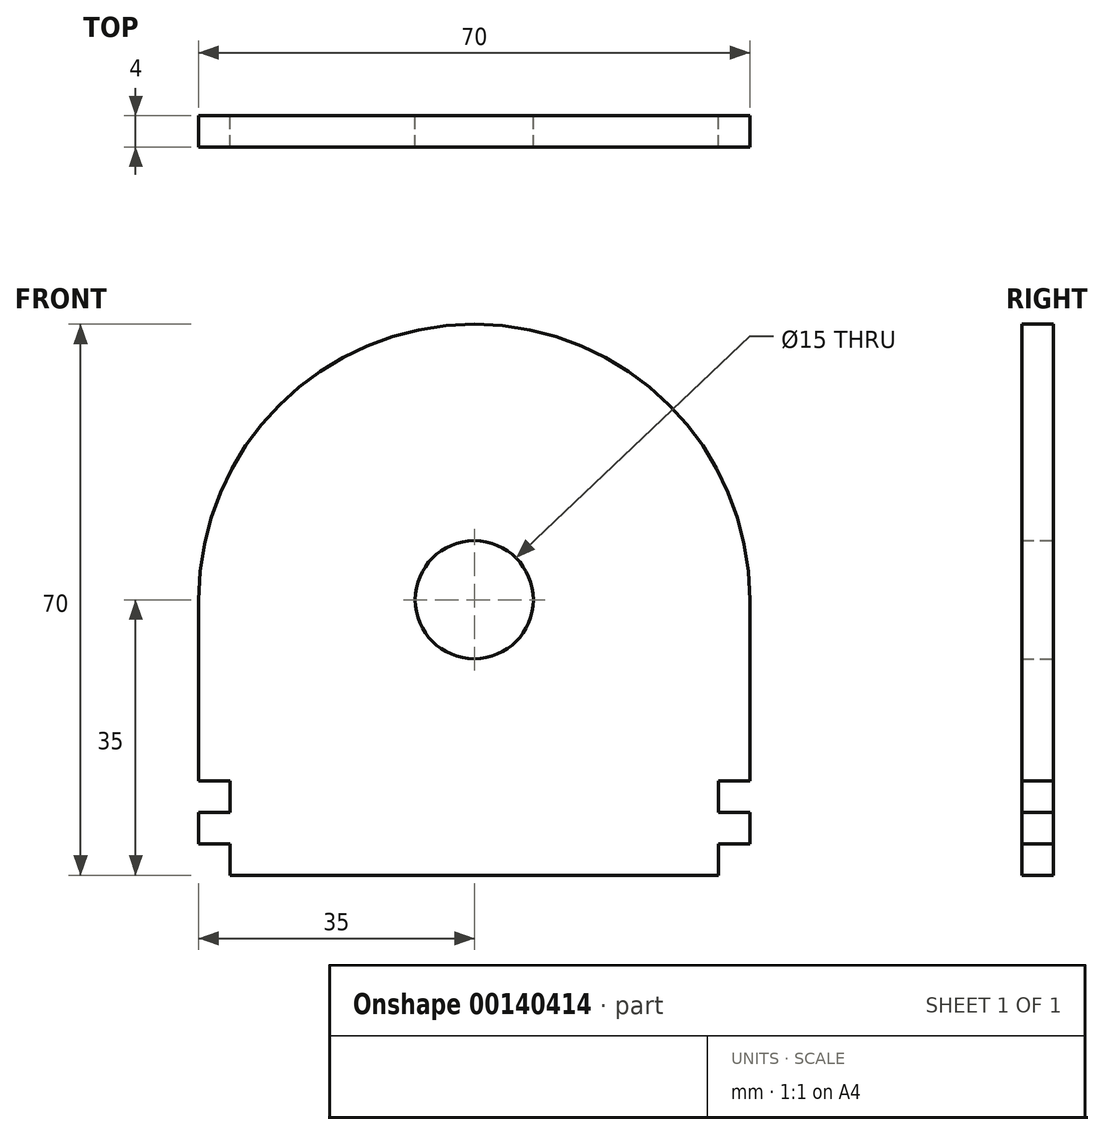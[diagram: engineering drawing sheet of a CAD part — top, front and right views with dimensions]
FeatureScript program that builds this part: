
annotation { "Feature Type Name" : "Feature", "Feature Type Description" : "" }
export const myFeature = defineFeature(function(context is Context, id is Id, definition is map)
    precondition{}
    {
        {
            var Q0;
            Q0=qCreatedBy(makeId("Front.planeOp"),FACE);
            var sketch = newSketch(context, id + "F0", { "sketchPlane" : qUnion([Q0])});
            skCircle(sketch, "E0", {"center": v(0, 0) * mm, "radius": 35 * mm});
            skLineSegment(sketch, "E1", {"start": v(0, -35) * mm, "end": v(35, -35) * mm});
            skLineSegment(sketch, "E2", {"start": v(35, -35) * mm, "end": v(35, 0) * mm});
            skLineSegment(sketch, "E3.MirrorCS", {"start": v(-35, -35) * mm, "end": v(-35, 0) * mm});
            skLineSegment(sketch, "E4.MirrorCS", {"start": v(0, -35) * mm, "end": v(-35, -35) * mm});
            skCircle(sketch, "E5", {"center": v(0, 0) * mm, "radius": 7.5 * mm});
            skLineSegment(sketch, "E6.bottom", {"start": v(-35, -35) * mm, "end": v(-31, -35) * mm});
            skLineSegment(sketch, "E6.top", {"start": v(-35, -31) * mm, "end": v(-31, -31) * mm});
            skLineSegment(sketch, "E6.left", {"start": v(-35, -35) * mm, "end": v(-35, -31) * mm});
            skLineSegment(sketch, "E6.right", {"start": v(-31, -35) * mm, "end": v(-31, -31) * mm});
            skLineSegment(sketch, "E7", {"start": v(-35, -31) * mm, "end": v(-35, -27) * mm});
            skLineSegment(sketch, "E8.bottom", {"start": v(-35, -27) * mm, "end": v(-31, -27) * mm});
            skLineSegment(sketch, "E8.top", {"start": v(-35, -23) * mm, "end": v(-31, -23) * mm});
            skLineSegment(sketch, "E8.left", {"start": v(-35, -27) * mm, "end": v(-35, -23) * mm});
            skLineSegment(sketch, "E8.right", {"start": v(-31, -27) * mm, "end": v(-31, -23) * mm});
            skLineSegment(sketch, "E9.MirrorCS", {"start": v(35, -23) * mm, "end": v(31, -23) * mm});
            skLineSegment(sketch, "E10.MirrorCS", {"start": v(31, -27) * mm, "end": v(31, -23) * mm});
            skLineSegment(sketch, "E11.MirrorCS", {"start": v(35, -27) * mm, "end": v(31, -27) * mm});
            skLineSegment(sketch, "E12.MirrorCS", {"start": v(35, -31) * mm, "end": v(31, -31) * mm});
            skLineSegment(sketch, "E13.MirrorCS", {"start": v(31, -35) * mm, "end": v(31, -31) * mm});
            skSolve(sketch);
        }
        {
            var Q0;
            Q0=makeQuery(id+"F0.imprint","IMPRINT",FACE,{"disambiguationData":[TD([[makeQuery(id+"F0.imprint","IMPRINT",EDGE,{"derivedFrom":sQuery(id+"F0.wireOp",EDGE,"E5")}),-1.0]])]});
            var Q1;
            {var subQ1=sQuery(id+"F0.wireOp",EDGE,"E3.MirrorCS");Q1=makeQuery(id+"F0.imprint","IMPRINT",FACE,{"disambiguationData":[TD([[makeQuery(id+"F0.imprint","IMPRINT",EDGE,{"derivedFrom":subQ1}),-1.0]])]});}
            var Q2;
            {var subQ3=sQuery(id+"F0.wireOp",EDGE,"E9.MirrorCS");Q2=makeQuery(id+"F0.imprint","IMPRINT",FACE,{"disambiguationData":[TD([[makeQuery(id+"F0.imprint","IMPRINT",EDGE,{"derivedFrom":subQ3}),-1.0]])]});}
            extrude(context, id + "F1", {"entities" : qUnion([Q0, Q1, Q2]), "depth" : 4 * mm});
        }
    });
